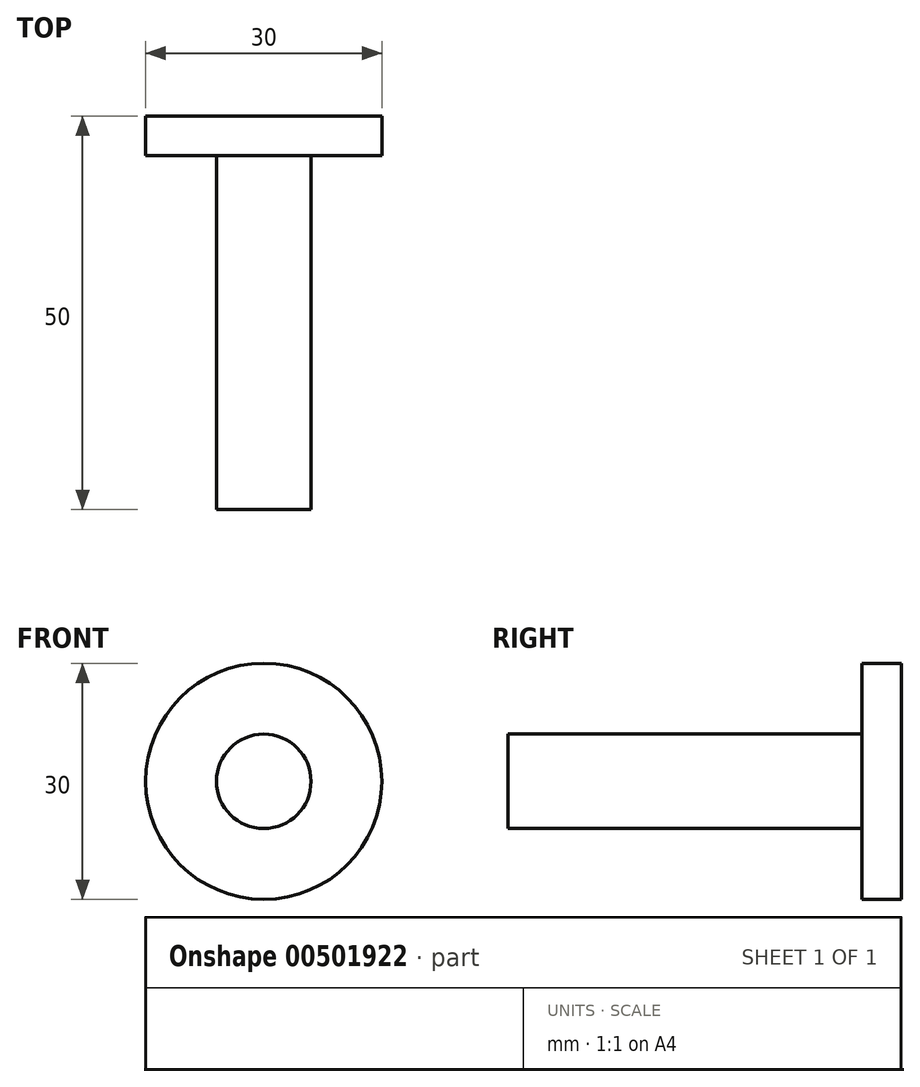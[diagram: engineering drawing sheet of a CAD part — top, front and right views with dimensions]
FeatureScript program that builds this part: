
annotation { "Feature Type Name" : "Feature", "Feature Type Description" : "" }
export const myFeature = defineFeature(function(context is Context, id is Id, definition is map)
    precondition{}
    {
        {
            var Q0;
            Q0=qCreatedBy(makeId("Front.planeOp"),FACE);
            var sketch = newSketch(context, id + "F0", { "sketchPlane" : qUnion([Q0])});
            skCircle(sketch, "E0", {"center": v(0, 0) * mm, "radius": 15 * mm});
            skSolve(sketch);
        }
        {
            var Q0;
            Q0=makeQuery(id+"F0.imprint","IMPRINT",FACE,{"disambiguationData":[TD([[makeQuery(id+"F0.imprint","IMPRINT",EDGE,{"derivedFrom":sQuery(id+"F0.wireOp",EDGE,"E0")}),1.0]])]});
            extrude(context, id + "F1", {"entities" : qUnion([Q0]), "depth" : 5 * mm});
        }
        {
            var Q0;
            Q0=qCreatedBy(makeId("Front.planeOp"),FACE);
            var sketch = newSketch(context, id + "F2", { "sketchPlane" : qUnion([Q0])});
            skCircle(sketch, "E1", {"center": v(0, 0) * mm, "radius": 6 * mm});
            skSolve(sketch);
        }
        {
            var Q0;
            Q0=makeQuery(id+"F2.imprint","IMPRINT",FACE,{"disambiguationData":[TD([[makeQuery(id+"F2.imprint","IMPRINT",EDGE,{"derivedFrom":sQuery(id+"F2.wireOp",EDGE,"E1")}),1.0]])]});
            var Q1;
            Q1=sQuery(id+"F2.wireOp",EDGE,"E1");
            extrude(context, id + "F3", {"entities" : qUnion([Q0]), "operationType" : NewBodyOperationType.ADD, "surfaceEntities" : qUnion([Q1]), "depth" : 50 * mm});
        }
    });
